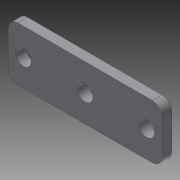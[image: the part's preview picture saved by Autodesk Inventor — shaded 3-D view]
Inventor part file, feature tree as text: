
AUTODESK INVENTOR PART (.ipt)
format: ipt  version: 2015 (Build 190159000, 159)  size: 94,208 bytes
history: native  units: in
note: dims shown in document units (in); Inventor stores cm internally (conversion verified against a paired STEP export)
features: extrude x1, sketch x1
ambient origin geometry x8: Origin, YZ Plane, XZ Plane, XY Plane, X Axis, Y Axis, Z Axis, Center Point
bodies: Solid1 (feature_tree)
feature tree (2):
  extrude  "Extrusion1"  Depth=1.378in
  sketch  "Sketch1"  dims[d0=3.937in d1=1.378in d2=3.1496in d3=0.4016in d4=0.25in d5=0.0in d6=0.4016in d7=0.25in]
